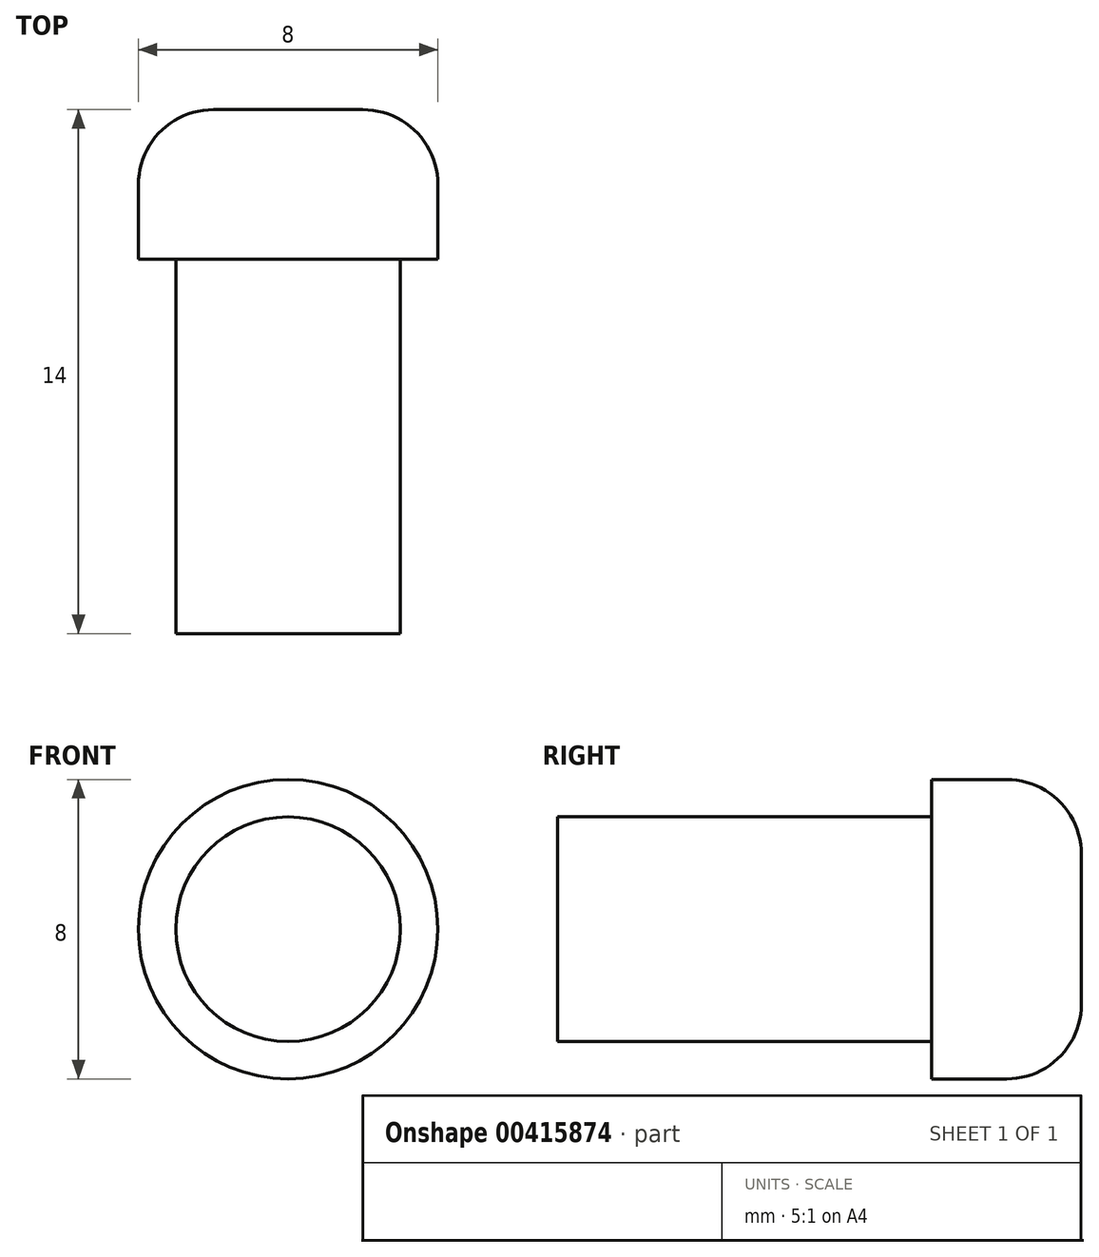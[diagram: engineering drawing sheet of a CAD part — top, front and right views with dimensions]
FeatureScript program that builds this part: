
annotation { "Feature Type Name" : "Feature", "Feature Type Description" : "" }
export const myFeature = defineFeature(function(context is Context, id is Id, definition is map)
    precondition{}
    {
        {
            var Q0;
            Q0=qCreatedBy(makeId("Front.planeOp"),FACE);
            var sketch = newSketch(context, id + "F0", { "sketchPlane" : qUnion([Q0])});
            skCircle(sketch, "E0", {"center": v(0, 0) * mm, "radius": 3 * mm});
            skCircle(sketch, "E1", {"center": v(0, 0) * mm, "radius": 4 * mm});
            skSolve(sketch);
        }
        {
            var Q0;
            Q0=makeQuery(id+"F0.imprint","IMPRINT",FACE,{"disambiguationData":[TD([[makeQuery(id+"F0.imprint","IMPRINT",EDGE,{"derivedFrom":sQuery(id+"F0.wireOp",EDGE,"E0")}),1.0]])]});
            extrude(context, id + "F1", {"entities" : qUnion([Q0]), "depth" : 10 * mm});
        }
        {
            var Q0;
            Q0=makeQuery(id+"F0.imprint","IMPRINT",FACE,{"disambiguationData":[TD([[makeQuery(id+"F0.imprint","IMPRINT",EDGE,{"derivedFrom":sQuery(id+"F0.wireOp",EDGE,"E0")}),-1.0]])]});
            var Q1;
            Q1=makeQuery(id+"F0.imprint","IMPRINT",FACE,{"disambiguationData":[TD([[makeQuery(id+"F0.imprint","IMPRINT",EDGE,{"derivedFrom":sQuery(id+"F0.wireOp",EDGE,"E0")}),1.0]])]});
            extrude(context, id + "F2", {"entities" : qUnion([Q0, Q1]), "operationType" : NewBodyOperationType.ADD, "oppositeDirection" : true, "depth" : 4 * mm});
        }
        {
            var Q0;
            Q0=makeQuery(id+"F2.opExtrude","CAP_EDGE",EDGE,{"disambiguationData":[OSD([sQuery(id+"F0.wireOp",EDGE,"E1")])],"isStart":false});
            fillet(context, id + "F3", {"entities" : qUnion([Q0]), "radius" : 2 * mm, "tangentPropagation" : true, "allowEdgeOverflow" : false});
        }
    });
